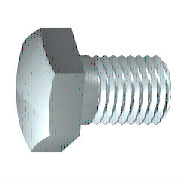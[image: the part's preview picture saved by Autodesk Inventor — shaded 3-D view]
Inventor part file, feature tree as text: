
AUTODESK INVENTOR PART (.ipt)
format: ipt  version: 2023.2 (Build 272271030, 271C)  size: 192,512 bytes
history: native  units: mm (DEFAULTED — no unit token found)
features: sketch x3, extrude x1, chamfer x1, plane x1
ambient origin geometry x7: Origin, YZ Plane, XZ Plane, X Axis, Y Axis, Z Axis, Center Point
bodies: Solid1 (feature_tree), Body (feature_tree)
feature tree (6):
  extrude  "Head"  Depth=22.0mm
  chamfer  "Chamfer1"  Distance=4.7mm
  plane  "Work Plane1"
  sketch  "Sketch1"  dims[d0=40.0mm d1=22.0mm]
  sketch  "Sketch2"  dims[d2=8.0mm]
  sketch  "Sketch4"  dims[d12=90.0deg d3=4.7mm d4=0.0mm d5=30.0deg d21=90.0deg d6=0.61345mm d7=0.61355mm d8=0.0mm d9=0.6001mm d10=11.63mm d11=13.0mm d13=0.61355mm d14=8.0mm d15=22.0mm d16=0.0mm d19=13.0mm d55=45.0deg d57=0.0mm d58=0.0mm]
